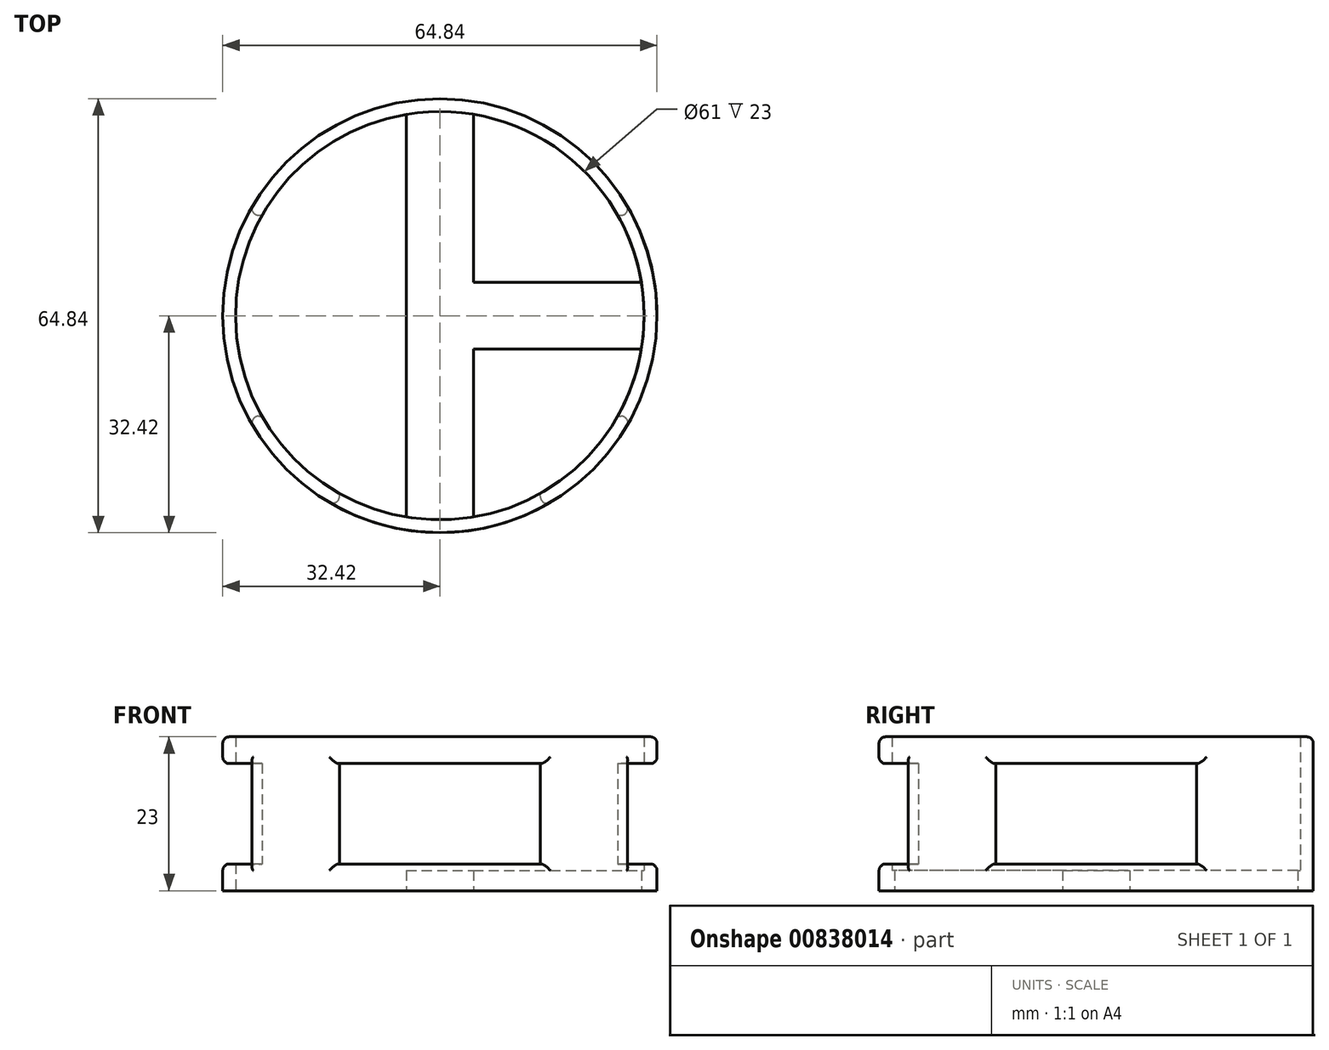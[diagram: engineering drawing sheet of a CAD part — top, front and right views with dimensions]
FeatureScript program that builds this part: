
annotation { "Feature Type Name" : "Feature", "Feature Type Description" : "" }
export const myFeature = defineFeature(function(context is Context, id is Id, definition is map)
    precondition{}
    {
        {
            var Q0;
            Q0=qCreatedBy(makeId("Top.planeOp"),FACE);
            var sketch = newSketch(context, id + "F0", { "sketchPlane" : qUnion([Q0])});
            skLineSegment(sketch, "E0.bottom", {"start": v(-5, 30.5) * mm, "end": v(5, 30.5) * mm});
            skLineSegment(sketch, "E0.top", {"start": v(-5, -30.5) * mm, "end": v(5, -30.5) * mm});
            skLineSegment(sketch, "E0.left", {"start": v(-5, 30.5) * mm, "end": v(-5, -30.5) * mm});
            skLineSegment(sketch, "E0.right", {"start": v(5, 30.5) * mm, "end": v(5, -30.5) * mm});
            skPoint(sketch, "E0.middle", {"position": v(0, 0) * mm});
            skLineSegment(sketch, "E1.top", {"start": v(-5, 32.42) * mm, "end": v(5, 32.42) * mm});
            skLineSegment(sketch, "E1.left", {"start": v(-5, 30.5) * mm, "end": v(-5, 32.42) * mm});
            skLineSegment(sketch, "E1.right", {"start": v(5, 30.5) * mm, "end": v(5, 32.42) * mm});
            skLineSegment(sketch, "E2", {"start": v(-5, 0) * mm, "end": v(5, 0) * mm, "construction": true});
            skLineSegment(sketch, "E3.MirrorCS", {"start": v(-5, -32.42) * mm, "end": v(5, -32.42) * mm});
            skLineSegment(sketch, "E4.MirrorCS", {"start": v(5, -30.5) * mm, "end": v(5, -32.42) * mm});
            skLineSegment(sketch, "E5.MirrorCS", {"start": v(-5, -30.5) * mm, "end": v(-5, -32.42) * mm});
            skLineSegment(sketch, "E6.bottom", {"start": v(-30.5, 5) * mm, "end": v(30.5, 5) * mm});
            skLineSegment(sketch, "E6.top", {"start": v(-30.5, -5) * mm, "end": v(30.5, -5) * mm});
            skLineSegment(sketch, "E6.left", {"start": v(-30.5, 5) * mm, "end": v(-30.5, -5) * mm});
            skLineSegment(sketch, "E6.right", {"start": v(30.5, 5) * mm, "end": v(30.5, -5) * mm});
            skLineSegment(sketch, "E7.bottom", {"start": v(-30.5, -5) * mm, "end": v(-32.42, -5) * mm});
            skLineSegment(sketch, "E7.top", {"start": v(-30.5, 5) * mm, "end": v(-32.42, 5) * mm});
            skLineSegment(sketch, "E7.left", {"start": v(-30.5, -5) * mm, "end": v(-30.5, 5) * mm});
            skLineSegment(sketch, "E7.right", {"start": v(-32.42, -5) * mm, "end": v(-32.42, 5) * mm});
            skLineSegment(sketch, "E8", {"start": v(0, -5) * mm, "end": v(0, 5) * mm, "construction": true});
            skLineSegment(sketch, "E9.MirrorCS", {"start": v(30.5, -5) * mm, "end": v(32.42, -5) * mm});
            skLineSegment(sketch, "E10.MirrorCS", {"start": v(32.42, -5) * mm, "end": v(32.42, 5) * mm});
            skLineSegment(sketch, "E11.MirrorCS", {"start": v(30.5, 5) * mm, "end": v(32.42, 5) * mm});
            skSolve(sketch);
        }
        {
            var Q0;
            {var subQ0=sQuery(id+"F0.wireOp",EDGE,"E6.bottom");var subQ1=sQuery(id+"F0.wireOp",EDGE,"E0.left");var subQ2=makeQuery(id+"F0.imprint","INTERSECT",VERTEX,{"derivedFrom":[subQ1,subQ0]});Q0=makeQuery(id+"F0.imprint","IMPRINT",FACE,{"disambiguationData":[TD([[makeQuery(id+"F0.imprint","IMPRINT",EDGE,{"disambiguationData":[TD([[subQ2,-1.0]])],"derivedFrom":subQ1}),1.0]])]});}
            var Q1;
            {var subQ0=sQuery(id+"F0.wireOp",EDGE,"E0.bottom");Q1=makeQuery(id+"F0.imprint","IMPRINT",FACE,{"disambiguationData":[TD([[makeQuery(id+"F0.imprint","IMPRINT",EDGE,{"derivedFrom":subQ0}),-1.0]])]});}
            var Q2;
            {var subQ5=sQuery(id+"F0.wireOp",EDGE,"E7.left");Q2=makeQuery(id+"F0.imprint","IMPRINT",FACE,{"disambiguationData":[TD([[makeQuery(id+"F0.imprint","IMPRINT",EDGE,{"derivedFrom":subQ5}),-1.0]])]});}
            var Q3;
            {var subQ5=sQuery(id+"F0.wireOp",EDGE,"E6.right");Q3=makeQuery(id+"F0.imprint","IMPRINT",FACE,{"disambiguationData":[TD([[makeQuery(id+"F0.imprint","IMPRINT",EDGE,{"derivedFrom":subQ5}),-1.0]])]});}
            var Q4;
            {var subQ0=sQuery(id+"F0.wireOp",EDGE,"E0.top");Q4=makeQuery(id+"F0.imprint","IMPRINT",FACE,{"disambiguationData":[TD([[makeQuery(id+"F0.imprint","IMPRINT",EDGE,{"derivedFrom":subQ0}),1.0]])]});}
            extrude(context, id + "F1", {"entities" : qUnion([Q0, Q1, Q2, Q3, Q4]), "depth" : 3 * mm, "offsetDistance" : 25 * mm});
        }
        {
            var Q0;
            Q0=makeQuery(id+"F1.opExtrude","CAP_FACE",FACE,{"disambiguationData":[OSD([sQuery(id+"F0.wireOp",EDGE,"E0.top"),sQuery(id+"F0.wireOp",EDGE,"E0.left"),sQuery(id+"F0.wireOp",EDGE,"E0.right"),sQuery(id+"F0.wireOp",EDGE,"E0.bottom"),sQuery(id+"F0.wireOp",EDGE,"E6.bottom"),sQuery(id+"F0.wireOp",EDGE,"E6.top"),sQuery(id+"F0.wireOp",EDGE,"E6.right"),sQuery(id+"F0.wireOp",EDGE,"E7.left")])],"isStart":false});
            var sketch = newSketch(context, id + "F2", { "sketchPlane" : qUnion([Q0])});
            skCircle(sketch, "E12", {"center": v(0, 0) * mm, "radius": 30.5 * mm});
            skCircle(sketch, "E13", {"center": v(0, 0) * mm, "radius": 32.42 * mm});
            skSolve(sketch);
        }
        {
            var Q0;
            {var subQ0=sQuery(id+"F2.wireOp",EDGE,"E12");var subQ1=sQuery(id+"F0.wireOp",EDGE,"E7.left");var subQ2=makeQuery(id+"F1.opExtrude","CAP_EDGE",EDGE,{"disambiguationData":[OSD([subQ1])],"isStart":false});var subQ3=makeQuery(id+"F2.imprint","INTERSECT",VERTEX,{"derivedFrom":[subQ2,subQ0]});Q0=makeQuery(id+"F2.imprint","IMPRINT",FACE,{"disambiguationData":[TD([[makeQuery(id+"F2.imprint","IMPRINT",EDGE,{"disambiguationData":[TD([[subQ3,-1.0]])],"derivedFrom":subQ0}),-1.0]])]});}
            var Q1;
            Q1=makeQuery(id+"F2.imprint","IMPRINT",FACE,{"disambiguationData":[TD([[makeQuery(id+"F2.imprint","IMPRINT",EDGE,{"derivedFrom":sQuery(id+"F2.wireOp",EDGE,"E13")}),1.0]])]});
            var Q2;
            {var subQ0=sQuery(id+"F2.wireOp",EDGE,"E12");var subQ1=sQuery(id+"F0.wireOp",EDGE,"E7.left");var subQ5=makeQuery(id+"F1.opExtrude","CAP_EDGE",EDGE,{"disambiguationData":[OSD([subQ1])],"isStart":false});var subQ6=makeQuery(id+"F2.imprint","INTERSECT",VERTEX,{"derivedFrom":[subQ5,subQ0]});Q2=makeQuery(id+"F2.imprint","IMPRINT",FACE,{"disambiguationData":[TD([[makeQuery(id+"F2.imprint","IMPRINT",EDGE,{"disambiguationData":[TD([[subQ6,1.0]])],"derivedFrom":subQ0}),-1.0]])]});}
            var Q3;
            {var subQ0=sQuery(id+"F2.wireOp",EDGE,"E12");var subQ1=sQuery(id+"F0.wireOp",EDGE,"E0.bottom");var subQ2=makeQuery(id+"F1.opExtrude","CAP_EDGE",EDGE,{"disambiguationData":[OSD([subQ1])],"isStart":false});var subQ3=makeQuery(id+"F2.imprint","INTERSECT",VERTEX,{"derivedFrom":[subQ2,subQ0]});Q3=makeQuery(id+"F2.imprint","IMPRINT",FACE,{"disambiguationData":[TD([[makeQuery(id+"F2.imprint","IMPRINT",EDGE,{"disambiguationData":[TD([[subQ3,-1.0]])],"derivedFrom":subQ0}),-1.0]])]});}
            var Q4;
            {var subQ0=sQuery(id+"F2.wireOp",EDGE,"E12");var subQ1=sQuery(id+"F0.wireOp",EDGE,"E0.bottom");var subQ5=makeQuery(id+"F1.opExtrude","CAP_EDGE",EDGE,{"disambiguationData":[OSD([subQ1])],"isStart":false});var subQ6=makeQuery(id+"F2.imprint","INTERSECT",VERTEX,{"derivedFrom":[subQ5,subQ0]});Q4=makeQuery(id+"F2.imprint","IMPRINT",FACE,{"disambiguationData":[TD([[makeQuery(id+"F2.imprint","IMPRINT",EDGE,{"disambiguationData":[TD([[subQ6,1.0]])],"derivedFrom":subQ0}),-1.0]])]});}
            var Q5;
            {var subQ0=sQuery(id+"F2.wireOp",EDGE,"E12");var subQ1=sQuery(id+"F0.wireOp",EDGE,"E6.right");var subQ2=makeQuery(id+"F1.opExtrude","CAP_EDGE",EDGE,{"disambiguationData":[OSD([subQ1])],"isStart":false});var subQ3=makeQuery(id+"F2.imprint","INTERSECT",VERTEX,{"derivedFrom":[subQ2,subQ0]});Q5=makeQuery(id+"F2.imprint","IMPRINT",FACE,{"disambiguationData":[TD([[makeQuery(id+"F2.imprint","IMPRINT",EDGE,{"disambiguationData":[TD([[subQ3,1.0]])],"derivedFrom":subQ0}),-1.0]])]});}
            var Q6;
            {var subQ0=sQuery(id+"F2.wireOp",EDGE,"E12");var subQ1=sQuery(id+"F0.wireOp",EDGE,"E6.right");var subQ5=makeQuery(id+"F1.opExtrude","CAP_EDGE",EDGE,{"disambiguationData":[OSD([subQ1])],"isStart":false});var subQ6=makeQuery(id+"F2.imprint","INTERSECT",VERTEX,{"derivedFrom":[subQ5,subQ0]});Q6=makeQuery(id+"F2.imprint","IMPRINT",FACE,{"disambiguationData":[TD([[makeQuery(id+"F2.imprint","IMPRINT",EDGE,{"disambiguationData":[TD([[subQ6,-1.0]])],"derivedFrom":subQ0}),-1.0]])]});}
            var Q7;
            {var subQ0=sQuery(id+"F2.wireOp",EDGE,"E12");var subQ2=sQuery(id+"F0.wireOp",EDGE,"E0.top");var subQ5=makeQuery(id+"F1.opExtrude","CAP_EDGE",EDGE,{"disambiguationData":[OSD([subQ2])],"isStart":false});var subQ6=makeQuery(id+"F2.imprint","INTERSECT",VERTEX,{"derivedFrom":[subQ5,subQ0]});Q7=makeQuery(id+"F2.imprint","IMPRINT",FACE,{"disambiguationData":[TD([[makeQuery(id+"F2.imprint","IMPRINT",EDGE,{"disambiguationData":[TD([[subQ6,1.0]])],"derivedFrom":subQ0}),-1.0]])]});}
            var Q8;
            {var subQ0=sQuery(id+"F2.wireOp",EDGE,"E12");var subQ1=sQuery(id+"F0.wireOp",EDGE,"E0.top");var subQ2=makeQuery(id+"F1.opExtrude","CAP_EDGE",EDGE,{"disambiguationData":[OSD([subQ1])],"isStart":false});var subQ3=makeQuery(id+"F2.imprint","INTERSECT",VERTEX,{"derivedFrom":[subQ2,subQ0]});Q8=makeQuery(id+"F2.imprint","IMPRINT",FACE,{"disambiguationData":[TD([[makeQuery(id+"F2.imprint","IMPRINT",EDGE,{"disambiguationData":[TD([[subQ3,-1.0]])],"derivedFrom":subQ0}),-1.0]])]});}
            extrude(context, id + "F3", {"entities" : qUnion([Q0, Q1, Q2, Q3, Q4, Q5, Q6, Q7, Q8]), "operationType" : NewBodyOperationType.ADD, "depth" : 20 * mm, "offsetDistance" : 25 * mm, "hasSecondDirection" : true, "secondDirectionOppositeDirection" : true, "secondDirectionDepth" : 3 * mm});
        }
        {
            var Q0;
            Q0=qCreatedBy(makeId("Front.planeOp"),FACE);
            var sketch = newSketch(context, id + "F4", { "sketchPlane" : qUnion([Q0])});
            skLineSegment(sketch, "E14.bottom", {"start": v(-15, 19) * mm, "end": v(15, 19) * mm});
            skLineSegment(sketch, "E14.top", {"start": v(-15, 4) * mm, "end": v(15, 4) * mm});
            skLineSegment(sketch, "E14.left", {"start": v(-15, 19) * mm, "end": v(-15, 4) * mm});
            skLineSegment(sketch, "E14.right", {"start": v(15, 19) * mm, "end": v(15, 4) * mm});
            skLineSegment(sketch, "E15", {"start": v(0, 4) * mm, "end": v(0, 19) * mm, "construction": true});
            skLineSegment(sketch, "E16", {"start": v(0, 0) * mm, "end": v(0, 4) * mm, "construction": true});
            skSolve(sketch);
        }
        {
            var Q0;
            Q0 = qSketchRegion(id + "F4", true);
            extrude(context, id + "F5", {"entities" : qUnion([Q0]), "operationType" : NewBodyOperationType.REMOVE, "endBound" : BoundingType.THROUGH_ALL, "depth" : 25 * mm, "offsetDistance" : 25 * mm});
        }
        {
            var Q0;
            Q0=qCreatedBy(makeId("Right.planeOp"),FACE);
            var sketch = newSketch(context, id + "F6", { "sketchPlane" : qUnion([Q0])});
            skLineSegment(sketch, "E17.bottom", {"start": v(-15, 19) * mm, "end": v(15, 19) * mm});
            skLineSegment(sketch, "E17.top", {"start": v(-15, 4) * mm, "end": v(15, 4) * mm});
            skLineSegment(sketch, "E17.left", {"start": v(-15, 19) * mm, "end": v(-15, 4) * mm});
            skLineSegment(sketch, "E17.right", {"start": v(15, 19) * mm, "end": v(15, 4) * mm});
            skLineSegment(sketch, "E18", {"start": v(0, 4) * mm, "end": v(0, 19) * mm, "construction": true});
            skLineSegment(sketch, "E19", {"start": v(0, 0) * mm, "end": v(0, 4) * mm, "construction": true});
            skSolve(sketch);
        }
        {
            var Q0;
            Q0=makeQuery(id+"F6.imprint","IMPRINT",FACE,{"disambiguationData":[TD([[makeQuery(id+"F6.imprint","IMPRINT",EDGE,{"derivedFrom":sQuery(id+"F6.wireOp",EDGE,"E17.bottom")}),-1.0]])]});
            extrude(context, id + "F7", {"entities" : qUnion([Q0]), "operationType" : NewBodyOperationType.REMOVE, "endBound" : BoundingType.THROUGH_ALL, "oppositeDirection" : true, "depth" : 25 * mm, "offsetDistance" : 25 * mm, "hasSecondDirection" : true, "secondDirectionBound" : SecondDirectionBoundingType.THROUGH_ALL, "secondDirectionOppositeDirection" : false, "secondDirectionDepth" : 25 * mm});
        }
        {
            var Q0;
            Q0=makeQuery(id+"F3.opExtrude","CAP_EDGE",EDGE,{"disambiguationData":[OSD([sQuery(id+"F2.wireOp",EDGE,"E13")])],"isStart":false});
            var Q1;
            Q1=makeQuery(id+"F7.boolean.opBoolean","INTERSECT",EDGE,{"disambiguationData":[OD(0.0)],"derivedFrom":[makeQuery(id+"F3.opExtrude","SWEPT_FACE",FACE,{"disambiguationData":[OSD([sQuery(id+"F2.wireOp",EDGE,"E13")])]}),makeQuery(id+"F7.opExtrude","SWEPT_FACE",FACE,{"disambiguationData":[OSD([sQuery(id+"F6.wireOp",EDGE,"E17.right")])]})]});
            var Q2;
            Q2=makeQuery(id+"F7.boolean.opBoolean","INTERSECT",EDGE,{"disambiguationData":[OD(0.0)],"derivedFrom":[makeQuery(id+"F3.opExtrude","SWEPT_FACE",FACE,{"disambiguationData":[OSD([sQuery(id+"F2.wireOp",EDGE,"E13")])]}),makeQuery(id+"F7.opExtrude","SWEPT_FACE",FACE,{"disambiguationData":[OSD([sQuery(id+"F6.wireOp",EDGE,"E17.top")])]})]});
            var Q3;
            Q3=makeQuery(id+"F7.boolean.opBoolean","INTERSECT",EDGE,{"disambiguationData":[OD(0.0)],"derivedFrom":[makeQuery(id+"F3.opExtrude","SWEPT_FACE",FACE,{"disambiguationData":[OSD([sQuery(id+"F2.wireOp",EDGE,"E13")])]}),makeQuery(id+"F7.opExtrude","SWEPT_FACE",FACE,{"disambiguationData":[OSD([sQuery(id+"F6.wireOp",EDGE,"E17.left")])]})]});
            var Q4;
            Q4=makeQuery(id+"F7.boolean.opBoolean","INTERSECT",EDGE,{"disambiguationData":[OD(0.0)],"derivedFrom":[makeQuery(id+"F3.opExtrude","SWEPT_FACE",FACE,{"disambiguationData":[OSD([sQuery(id+"F2.wireOp",EDGE,"E13")])]}),makeQuery(id+"F7.opExtrude","SWEPT_FACE",FACE,{"disambiguationData":[OSD([sQuery(id+"F6.wireOp",EDGE,"E17.bottom")])]})]});
            var Q5;
            Q5=makeQuery(id+"F5.boolean.opBoolean","INTERSECT",EDGE,{"disambiguationData":[OD(0.0)],"derivedFrom":[makeQuery(id+"F3.opExtrude","SWEPT_FACE",FACE,{"disambiguationData":[OSD([sQuery(id+"F2.wireOp",EDGE,"E13")])]}),makeQuery(id+"F5.opExtrude","SWEPT_FACE",FACE,{"disambiguationData":[OSD([sQuery(id+"F4.wireOp",EDGE,"E14.top")])]})]});
            var Q6;
            Q6=makeQuery(id+"F5.boolean.opBoolean","INTERSECT",EDGE,{"disambiguationData":[OD(0.0)],"derivedFrom":[makeQuery(id+"F3.opExtrude","SWEPT_FACE",FACE,{"disambiguationData":[OSD([sQuery(id+"F2.wireOp",EDGE,"E13")])]}),makeQuery(id+"F5.opExtrude","SWEPT_FACE",FACE,{"disambiguationData":[OSD([sQuery(id+"F4.wireOp",EDGE,"E14.left")])]})]});
            var Q7;
            Q7=makeQuery(id+"F5.boolean.opBoolean","INTERSECT",EDGE,{"disambiguationData":[OD(0.0)],"derivedFrom":[makeQuery(id+"F3.opExtrude","SWEPT_FACE",FACE,{"disambiguationData":[OSD([sQuery(id+"F2.wireOp",EDGE,"E13")])]}),makeQuery(id+"F5.opExtrude","SWEPT_FACE",FACE,{"disambiguationData":[OSD([sQuery(id+"F4.wireOp",EDGE,"E14.bottom")])]})]});
            var Q8;
            Q8=makeQuery(id+"F5.boolean.opBoolean","INTERSECT",EDGE,{"disambiguationData":[OD(0.0)],"derivedFrom":[makeQuery(id+"F3.opExtrude","SWEPT_FACE",FACE,{"disambiguationData":[OSD([sQuery(id+"F2.wireOp",EDGE,"E13")])]}),makeQuery(id+"F5.opExtrude","SWEPT_FACE",FACE,{"disambiguationData":[OSD([sQuery(id+"F4.wireOp",EDGE,"E14.right")])]})]});
            var Q9;
            Q9=makeQuery(id+"F7.boolean.opBoolean","INTERSECT",EDGE,{"disambiguationData":[OD(1.0)],"derivedFrom":[makeQuery(id+"F3.opExtrude","SWEPT_FACE",FACE,{"disambiguationData":[OSD([sQuery(id+"F2.wireOp",EDGE,"E13")])]}),makeQuery(id+"F7.opExtrude","SWEPT_FACE",FACE,{"disambiguationData":[OSD([sQuery(id+"F6.wireOp",EDGE,"E17.top")])]})]});
            var Q10;
            Q10=makeQuery(id+"F7.boolean.opBoolean","INTERSECT",EDGE,{"disambiguationData":[OD(1.0)],"derivedFrom":[makeQuery(id+"F3.opExtrude","SWEPT_FACE",FACE,{"disambiguationData":[OSD([sQuery(id+"F2.wireOp",EDGE,"E13")])]}),makeQuery(id+"F7.opExtrude","SWEPT_FACE",FACE,{"disambiguationData":[OSD([sQuery(id+"F6.wireOp",EDGE,"E17.left")])]})]});
            var Q11;
            Q11=makeQuery(id+"F7.boolean.opBoolean","INTERSECT",EDGE,{"disambiguationData":[OD(1.0)],"derivedFrom":[makeQuery(id+"F3.opExtrude","SWEPT_FACE",FACE,{"disambiguationData":[OSD([sQuery(id+"F2.wireOp",EDGE,"E13")])]}),makeQuery(id+"F7.opExtrude","SWEPT_FACE",FACE,{"disambiguationData":[OSD([sQuery(id+"F6.wireOp",EDGE,"E17.bottom")])]})]});
            var Q12;
            Q12=makeQuery(id+"F7.boolean.opBoolean","INTERSECT",EDGE,{"disambiguationData":[OD(1.0)],"derivedFrom":[makeQuery(id+"F3.opExtrude","SWEPT_FACE",FACE,{"disambiguationData":[OSD([sQuery(id+"F2.wireOp",EDGE,"E13")])]}),makeQuery(id+"F7.opExtrude","SWEPT_FACE",FACE,{"disambiguationData":[OSD([sQuery(id+"F6.wireOp",EDGE,"E17.right")])]})]});
            var Q13;
            Q13=makeQuery(id+"F5.boolean.opBoolean","INTERSECT",EDGE,{"disambiguationData":[OD(1.0)],"derivedFrom":[makeQuery(id+"F3.opExtrude","SWEPT_FACE",FACE,{"disambiguationData":[OSD([sQuery(id+"F2.wireOp",EDGE,"E13")])]}),makeQuery(id+"F5.opExtrude","SWEPT_FACE",FACE,{"disambiguationData":[OSD([sQuery(id+"F4.wireOp",EDGE,"E14.right")])]})]});
            var Q14;
            Q14=makeQuery(id+"F5.boolean.opBoolean","INTERSECT",EDGE,{"disambiguationData":[OD(1.0)],"derivedFrom":[makeQuery(id+"F3.opExtrude","SWEPT_FACE",FACE,{"disambiguationData":[OSD([sQuery(id+"F2.wireOp",EDGE,"E13")])]}),makeQuery(id+"F5.opExtrude","SWEPT_FACE",FACE,{"disambiguationData":[OSD([sQuery(id+"F4.wireOp",EDGE,"E14.top")])]})]});
            var Q15;
            Q15=makeQuery(id+"F5.boolean.opBoolean","INTERSECT",EDGE,{"disambiguationData":[OD(1.0)],"derivedFrom":[makeQuery(id+"F3.opExtrude","SWEPT_FACE",FACE,{"disambiguationData":[OSD([sQuery(id+"F2.wireOp",EDGE,"E13")])]}),makeQuery(id+"F5.opExtrude","SWEPT_FACE",FACE,{"disambiguationData":[OSD([sQuery(id+"F4.wireOp",EDGE,"E14.left")])]})]});
            var Q16;
            Q16=makeQuery(id+"F5.boolean.opBoolean","INTERSECT",EDGE,{"disambiguationData":[OD(1.0)],"derivedFrom":[makeQuery(id+"F3.opExtrude","SWEPT_FACE",FACE,{"disambiguationData":[OSD([sQuery(id+"F2.wireOp",EDGE,"E13")])]}),makeQuery(id+"F5.opExtrude","SWEPT_FACE",FACE,{"disambiguationData":[OSD([sQuery(id+"F4.wireOp",EDGE,"E14.bottom")])]})]});
            fillet(context, id + "F8", {"entities" : qUnion([Q0, Q1, Q2, Q3, Q4, Q5, Q6, Q7, Q8, Q9, Q10, Q11, Q12, Q13, Q14, Q15, Q16]), "radius" : 1 * mm, "tangentPropagation" : true, "allowEdgeOverflow" : false});
        }
    });
